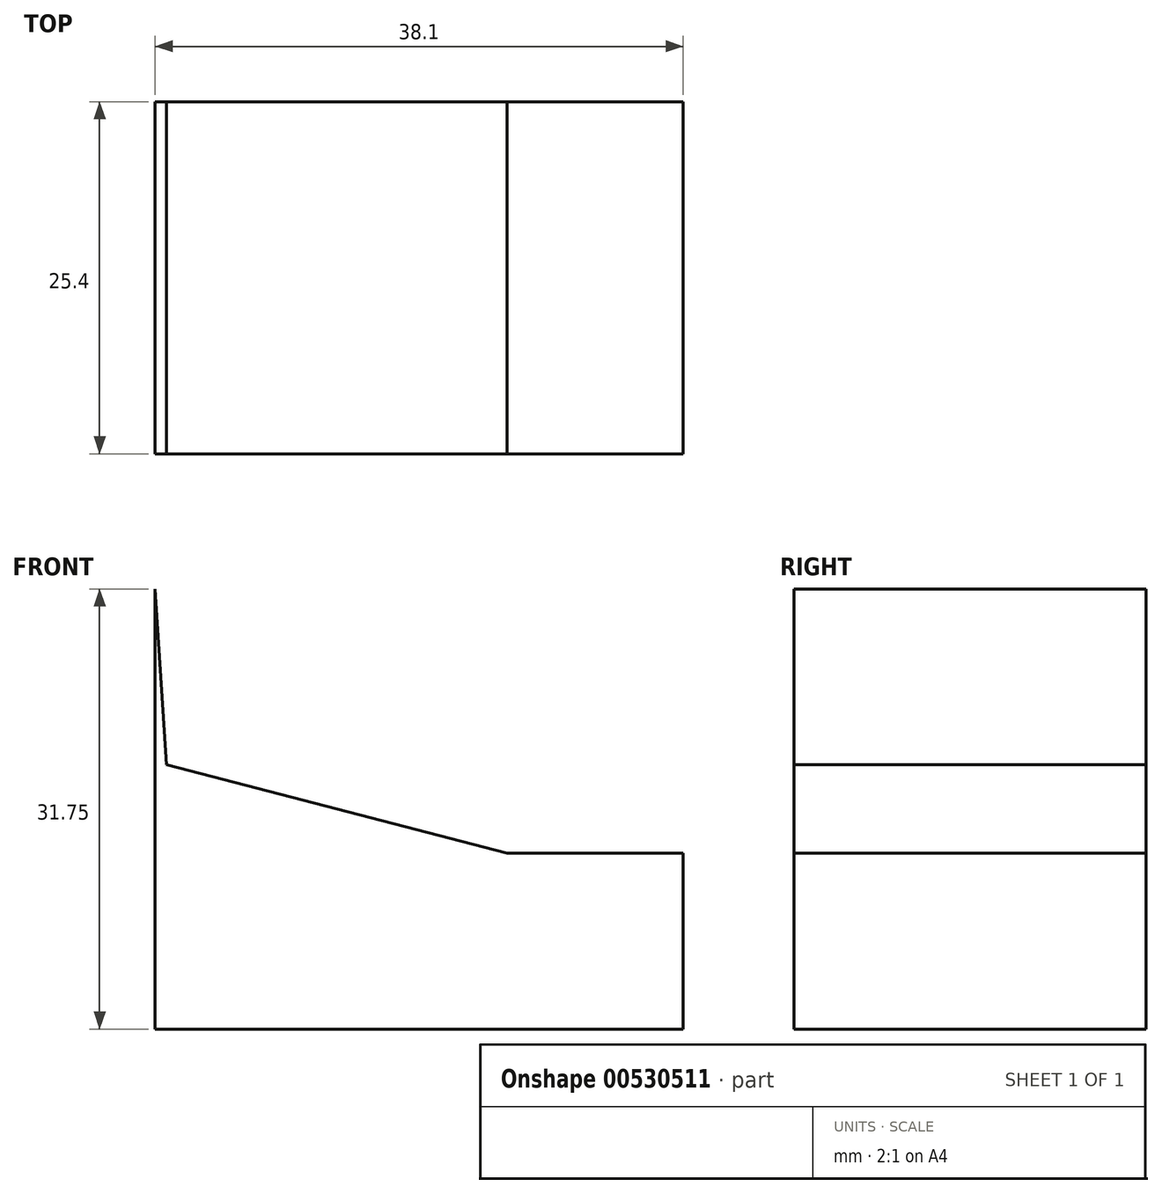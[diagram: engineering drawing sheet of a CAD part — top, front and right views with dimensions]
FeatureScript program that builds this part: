
annotation { "Feature Type Name" : "Feature", "Feature Type Description" : "" }
export const myFeature = defineFeature(function(context is Context, id is Id, definition is map)
    precondition{}
    {
        {
            var Q0;
            Q0=qCreatedBy(makeId("Front.planeOp"),FACE);
            var sketch = newSketch(context, id + "F0", { "sketchPlane" : qUnion([Q0])});
            skLineSegment(sketch, "E0", {"start": v(-10.07, 10.81) * mm, "end": v(-10.07, -20.94) * mm});
            skLineSegment(sketch, "E1", {"start": v(-10.07, -20.94) * mm, "end": v(28.03, -20.94) * mm});
            skLineSegment(sketch, "E2", {"start": v(28.03, -20.94) * mm, "end": v(28.03, -8.24) * mm});
            skLineSegment(sketch, "E3", {"start": v(28.03, -8.24) * mm, "end": v(15.33, -8.24) * mm});
            skLineSegment(sketch, "E4", {"start": v(15.33, -8.24) * mm, "end": v(-9.26, -1.86) * mm});
            skLineSegment(sketch, "E5", {"start": v(-9.26, -1.86) * mm, "end": v(-10.07, 10.81) * mm});
            skSolve(sketch);
        }
        {
            var Q0;
            Q0=makeQuery(id+"F0.imprint","IMPRINT",FACE,{"disambiguationData":[TD([[makeQuery(id+"F0.imprint","IMPRINT",EDGE,{"derivedFrom":sQuery(id+"F0.wireOp",EDGE,"E0")}),1.0]])]});
            extrude(context, id + "F1", {"entities" : qUnion([Q0]), "depth" : 25.4 * mm, "offsetDistance" : 25.4 * mm});
        }
    });
